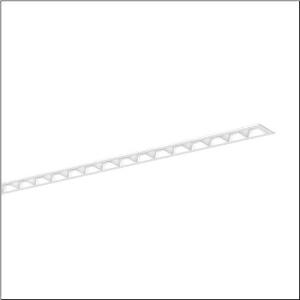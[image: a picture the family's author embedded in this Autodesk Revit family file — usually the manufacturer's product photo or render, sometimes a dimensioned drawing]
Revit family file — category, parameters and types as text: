
# Revit family: silica_r__21_51mx16dc3awb_c0f3
name_source: partatom
category: Lighting Fixtures
units: mm (PartAtom-declared; Revit-internal decimal feet)

## family parameters
Cut with Voids When Loaded = No
Host = Face
Light Source = No
Part Type = Normal
Room Calculation Point = No
Round Connector Dimension = Use Diameter
Shared = No

## types (1)
- --- (1 x LED, 10800 lm, 63.6 W, 3000K)
    Apparent Load = 64 VA
    CIE Flux Codes = 83 98 100 100 100
    Color Rendering = 80
    Color Temperature = 3000K
    Default Elevation = 1800 mm
    Description = Silica® 21, office luminaire, primary light control with darklight reflector, of PMMA, white, CAT 2 (L<= 3000cd/m²), light emission: direct distribution, primary light characteristic: symmetric, installation type: recessed, LED, rated luminous flux: 10.800lm, luminous efficacy: 170lm/W, light colour: 830, colour temperature: 3000K, with terminal, 3+2-pole, max. 2.5mm², mains connection: 220..240V, AC, 50/60Hz, rated input power: 63.6W, luminaire housing, of aluminium, traffic white (RAL 9016), length: 3.028mm, width: 79mm, height: 53mm, protection rating (complete): IP20, insulation class (complete): insulation class I (protective earthing), certification: CE, permissible operating ambient temperature: 0..+35°C, standard: EN 50419, packaging unit: 1 piece
    Height = 0 mm  [stored 0 ft]
    Lamp = 1 x LED
    Lamp Light Flux = 10800 lm
    Lamp Power = 63.6 W
    Lamp count = 1
    Length = 3027 mm
    Luminous efficacy = 170 lm/W
    Manufacturer = Siteco
    ModVariant = No
    Model = 51MX16DC3AWB
    Mounting Place = Ceiling
    Mounting Type = Recessed
    Number of Poles = 1
    OnlyDefault = Yes
    Power Factor = 1
    Product Name = Silica® 21
    Product group = office luminaire | ceiling recessed
    ProductGroupID = 401
    Protection Class = Protection class I
    Protection Degree = IP 20
    RLX_Detail_Level = 1
    RLX_Emergency_Light_Flux = 0 lm
    RLX_Emergency_Type = 0
    RLX_Emergency_Type_DB = No
    RlxData = <blob elided: 60297 chars, md5=4ef6c6ca>
    Socket = socket
    Standby Power = 0 W
    System Light Flux = 10800 lm
    System Power = 64 W
    Type Comments = factory setting: luminous flux: 100 % | dim-lin: 254 | 360 mA
    Type Image = l_1313606.jpg
    URL = http://relux.com
    VarID = @adj_073189
    Voltage = 0 V
    Weight = 0.00 kg
    Width = 79 mm

note: [stored X ft] marks values corroborated as IEEE doubles in the binary element streams (Revit-internal decimal feet)

## geometry (parser evidence)
native form markers: Blend x4, Sweep x12
no freeform markers — native parametric forms only
